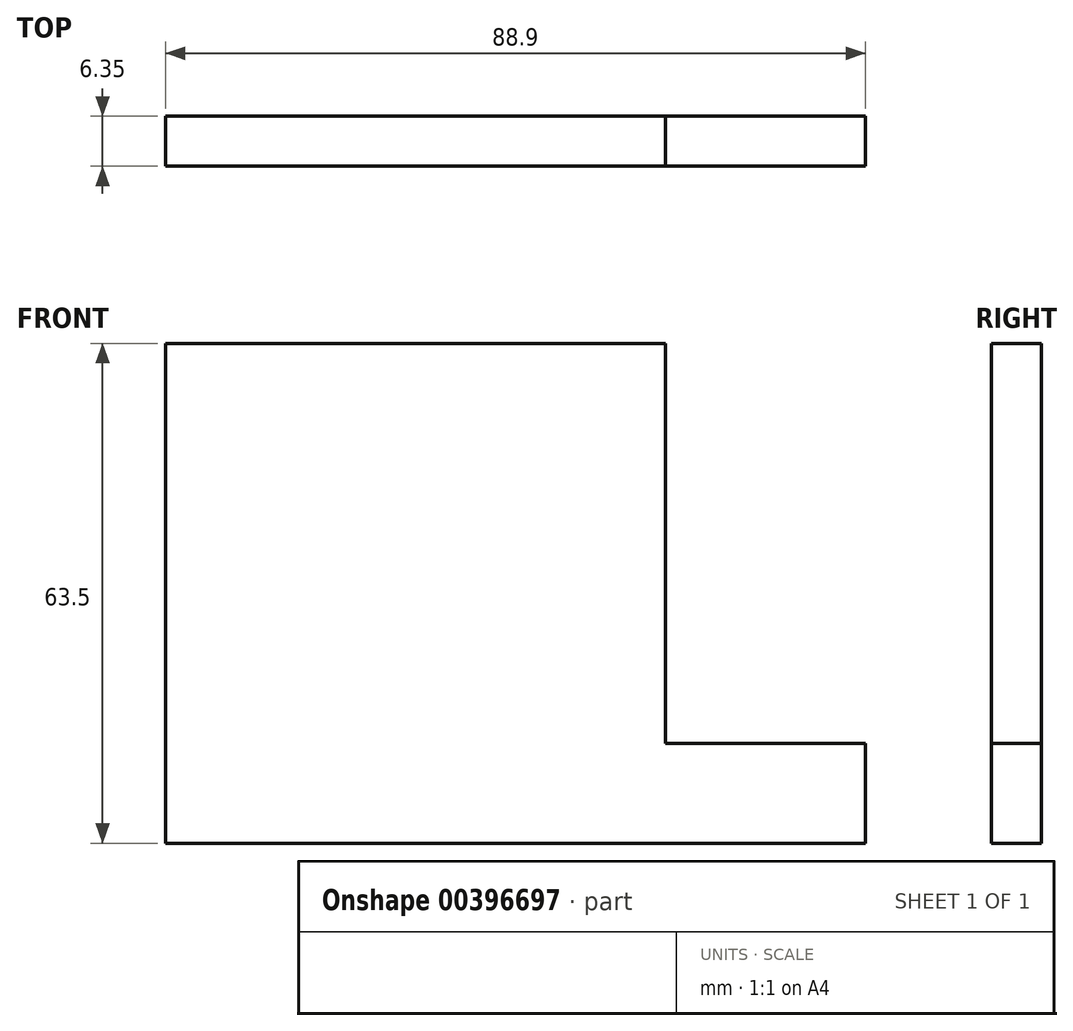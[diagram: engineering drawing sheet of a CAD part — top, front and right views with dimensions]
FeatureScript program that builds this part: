
annotation { "Feature Type Name" : "Feature", "Feature Type Description" : "" }
export const myFeature = defineFeature(function(context is Context, id is Id, definition is map)
    precondition{}
    {
        {
            var Q0;
            Q0=qCreatedBy(makeId("Front.planeOp"),FACE);
            var sketch = newSketch(context, id + "F0", { "sketchPlane" : qUnion([Q0])});
            skLineSegment(sketch, "E0.bottom", {"start": v(0, 0) * mm, "end": v(-63.5, 0) * mm});
            skLineSegment(sketch, "E0.top", {"start": v(0, 63.5) * mm, "end": v(-63.5, 63.5) * mm});
            skLineSegment(sketch, "E0.left", {"start": v(0, 12.7) * mm, "end": v(0, 63.5) * mm});
            skLineSegment(sketch, "E0.right", {"start": v(-63.5, 0) * mm, "end": v(-63.5, 63.5) * mm});
            skLineSegment(sketch, "E1.bottom", {"start": v(0, 0) * mm, "end": v(25.4, 0) * mm});
            skLineSegment(sketch, "E1.top", {"start": v(0, 12.7) * mm, "end": v(25.4, 12.7) * mm});
            skLineSegment(sketch, "E1.right", {"start": v(25.4, 0) * mm, "end": v(25.4, 12.7) * mm});
            skSolve(sketch);
        }
        {
            var Q0;
            Q0 = qSketchRegion(id + "F0", true);
            extrude(context, id + "F1", {"entities" : qUnion([Q0]), "depth" : 6.35 * mm});
        }
    });
